# Revit family: 51852183
name_source: partatom
category: Plumbing Fixtures
revit_build: Autodesk Revit 2018 (Build: 20170223_1515(x64)
units: mm (PartAtom-declared; Revit-internal decimal feet)

## family parameters
Always vertical = Yes
Cut with Voids When Loaded = No
OmniClass Number = 23.45.55.00
OmniClass Title = Sanitary Faucets, Wastes
Part Type = Normal
Room Calculation Point = No
Round Connector Dimension = Use Diameter
Shared = No
Work Plane-Based = No

## types (1)
- 51852183 Bath and shower faucet
    2D/3D/BIM Files URL = http://static.hansa.com
    3D View = https://static.hansa.com
    Additional Features = protected against back-flow in domestic use (according to DIN EN 1717)
    Aerator = Standard aerator
    AssetType = Fixed
    BIMObjectName = 51852183
    Backflow Prevention EN1717 = EB
    BodyMaterial = Brass
    Brand = HANSA
    Catalog Drawing URL = http://static.hansa.com
    Category = Bathroom
    CloseOffRating = 0
    Color = Chrome
    Connection = Ball eccentric coupling(s)
    Connection Size = G1/2
    Dimension Drawing URL = http://static.hansa.com
    Diverter = Push operated diverter;Integrated into spout;Automatic reset
    DurationUnit = Year
    EAN Number = 4057304006722
    EN Standard = EN 817
    ETIM Class Number = EC010862 Bath mixing tap
    FDV Document URL = http://www.hansa.com
    FaucetMainMaterial = Brass
    Features = Single-lever, side operated
    Finish = Polished
    Flow Drawing URL = http://static.hansa.com
    Flow Rate At 300kPa = 34.0 L/s
    FlowCoefficient = 0
    Group = Bath and shower faucet
    HWFU = 0
    IfcExportAs = IfcValveType
    IfcExportType = FAUCET
    Installation Type = Wall mounted
    Installation Width = CC150 ± 15 mm
    Installation and Maintenance Guide URL = http://static.hansa.com
    Interactive AR View URL = https://static.hansa.com
    Lever Handle = Single operating lever/handle;Hot/Cold symbols
    Manufacturer = HANSA
    ManufacturerName = HANSA
    ManufacturerURL = http://www.hansa.com
    Market = International;Germany;Austria;Belgium;Netherlands;France;Czech Republic;Slovakia;Spain
    Material = Brass
    Max. Hot Water Supply = 80 °C
    Mechanical Parts = Non-return valve(s);ø 40 mm ceramic cartridge for flow and temperature control
    Mobile Product Information URL = http://mpi.hansa.com
    Model = 51852183 Bath and shower faucet
    ModelReference = 51852183
    NBSDescription = Water supply fittings for baths
    NBSReference = 45-35-70/315
    Name = 51852183 Bath and shower faucet
    Name_en = 51852183 Bath and shower faucet
    Noise Class = II (ISO 3822)
    NominalDepth = 173 mm  [stored 0.567585 ft]
    NominalHeight = 109 mm  [stored 0.357612 ft]
    NominalWidth = 305 mm
    Pressure Loss With Flow 02ls = 150000.0 Pa
    Pressure Loss With Flow 03ls = 300000.0 Pa
    Product Code = 51852183
    Product Family = HANSADESIGNO Style
    Product Image URL = http://static.hansa.com
    Product URL = http://static.hansa.com
    ProductInformation = Single-lever bath mixer
    Revision = 4
    Sales Package dimensions (LxWxH) = 363 x 215 x 140
    Shape = Sculptured
    Short Marketing = single-lever bath mixer, DN 15 G1/2
    Size = 304.5x173x109 mm
    Spare-Part Information URL = http://static.hansa.com
    Spout Projection = 146 mm
    Surface treatment = Chrome
    Technical DataSheet URL = http://www.hansa.com
    Temperature = Temperature limiter;Temperature limiter (retrofittable)
    Temperature Adjustments = Limitation option for maximum temperature and flow-rate ;Adjustable hot water stop (included, retrofittable)
    UNSPSC Class Number = 30181700 Faucets or taps
    URL Declaration of Conformity = http://static.hansa.com
    URL REACH = http://static.hansa.com
    Uniclass2 = Pr_40_30_96_07
    Uniclass2015Description = Bath manual water supply sets
    Uniclass2015Reference = Pr_40_20_87_07
    Version = 4
    VersionDate = 01/07/2022
    Warranty Information URL = http://warranty.hansa.com
    WarrantyDescription = http://warranty.hansa.com
    WarrantyDurationUnit = Year
    Working Pressure = 50 - 1000 kPa
    WorkingPressure = 50 - 1000 kPa

note: [stored X ft] marks values corroborated as IEEE doubles in the binary element streams (Revit-internal decimal feet)

## geometry (parser evidence)
native form markers: Sweep x5
no freeform markers — native parametric forms only
